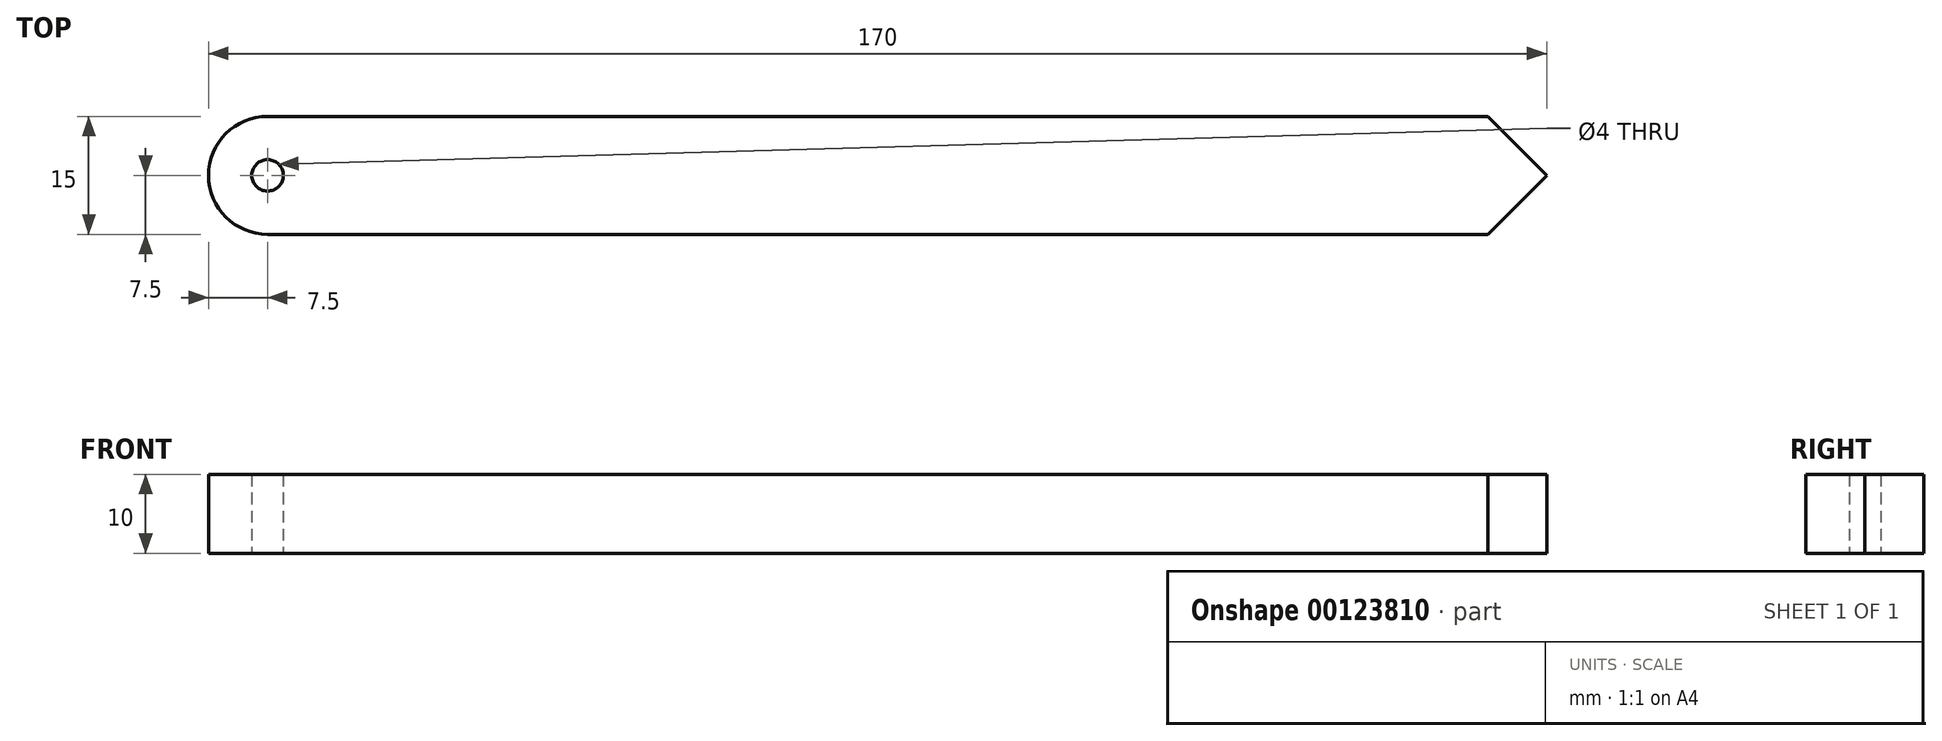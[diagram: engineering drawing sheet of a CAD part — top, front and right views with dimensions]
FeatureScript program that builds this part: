
annotation { "Feature Type Name" : "Feature", "Feature Type Description" : "" }
export const myFeature = defineFeature(function(context is Context, id is Id, definition is map)
    precondition{}
    {
        {
            var Q0;
            Q0=qCreatedBy(makeId("Top.planeOp"),FACE);
            var sketch = newSketch(context, id + "F0", { "sketchPlane" : qUnion([Q0])});
            skLineSegment(sketch, "E0.bottom", {"start": v(-85, 7.5) * mm, "end": v(85, 7.5) * mm});
            skLineSegment(sketch, "E0.top", {"start": v(-85, -7.5) * mm, "end": v(85, -7.5) * mm});
            skLineSegment(sketch, "E0.left", {"start": v(-85, 7.5) * mm, "end": v(-85, -7.5) * mm});
            skLineSegment(sketch, "E0.right", {"start": v(85, 7.5) * mm, "end": v(85, -7.5) * mm});
            skPoint(sketch, "E0.middle", {"position": v(0, 0) * mm});
            skArc(sketch, "E1", {"start": v(-85, 7.5) * mm, "mid": v(-92.5, 0) * mm, "end": v(-85, -7.5) * mm});
            skCircle(sketch, "E2", {"center": v(-85, 0) * mm, "radius": 2 * mm});
            skLineSegment(sketch, "E3", {"start": v(85, -7.5) * mm, "end": v(70, 7.5) * mm});
            skLineSegment(sketch, "E4", {"start": v(77.5, 0) * mm, "end": v(70, -7.5) * mm});
            skSolve(sketch);
        }
        {
            var Q0;
            {var subQ6=sQuery(id+"F0.wireOp",EDGE,"E4");Q0=makeQuery(id+"F0.imprint","IMPRINT",FACE,{"disambiguationData":[TD([[makeQuery(id+"F0.imprint","IMPRINT",EDGE,{"derivedFrom":subQ6}),-1.0]])]});}
            var Q1;
            {var subQ0=sQuery(id+"F0.wireOp",EDGE,"E1");Q1=makeQuery(id+"F0.imprint","IMPRINT",FACE,{"disambiguationData":[TD([[makeQuery(id+"F0.imprint","IMPRINT",EDGE,{"derivedFrom":subQ0}),1.0]])]});}
            extrude(context, id + "F1", {"entities" : qUnion([Q0, Q1]), "depth" : 10 * mm});
        }
    });
